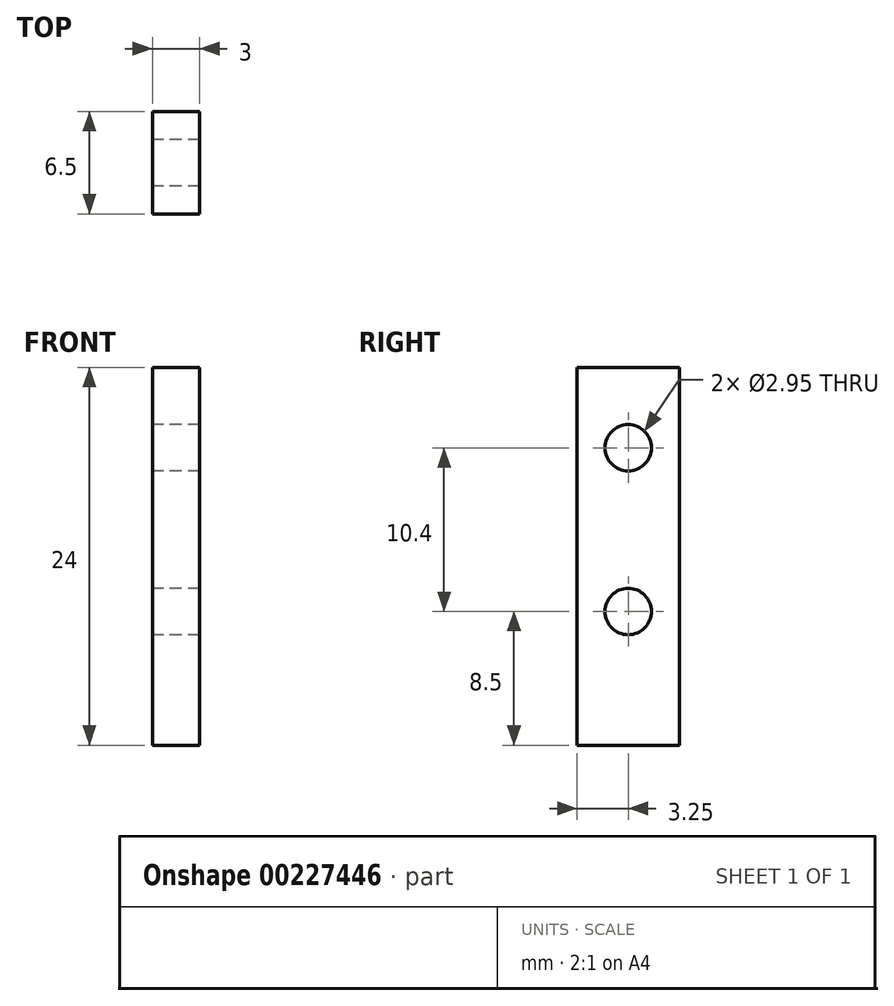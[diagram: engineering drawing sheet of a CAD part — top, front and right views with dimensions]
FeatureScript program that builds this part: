
annotation { "Feature Type Name" : "Feature", "Feature Type Description" : "" }
export const myFeature = defineFeature(function(context is Context, id is Id, definition is map)
    precondition{}
    {
        {
            var Q0;
            Q0=qCreatedBy(makeId("Right.planeOp"),FACE);
            var sketch = newSketch(context, id + "F0", { "sketchPlane" : qUnion([Q0])});
            skLineSegment(sketch, "E0.bottom", {"start": v(3.25, -12) * mm, "end": v(-3.25, -12) * mm});
            skLineSegment(sketch, "E0.top", {"start": v(3.25, 12) * mm, "end": v(-3.25, 12) * mm});
            skLineSegment(sketch, "E0.left", {"start": v(3.25, -12) * mm, "end": v(3.25, 12) * mm});
            skLineSegment(sketch, "E0.right", {"start": v(-3.25, -12) * mm, "end": v(-3.25, 12) * mm});
            skPoint(sketch, "E0.middle", {"position": v(0, 0) * mm});
            skPoint(sketch, "E1", {"position": v(0, -3.5) * mm});
            skPoint(sketch, "E2", {"position": v(0, 6.9) * mm});
            skCircle(sketch, "E3", {"center": v(0, -3.5) * mm, "radius": 1.48 * mm});
            skCircle(sketch, "E4", {"center": v(0, 6.9) * mm, "radius": 1.48 * mm});
            skSolve(sketch);
        }
        {
            var Q0;
            Q0=makeQuery(id+"F0.imprint","IMPRINT",FACE,{"disambiguationData":[TD([[makeQuery(id+"F0.imprint","IMPRINT",EDGE,{"derivedFrom":sQuery(id+"F0.wireOp",EDGE,"E0.bottom")}),-1.0]])]});
            extrude(context, id + "F1", {"entities" : qUnion([Q0]), "depth" : 3 * mm});
        }
    });
